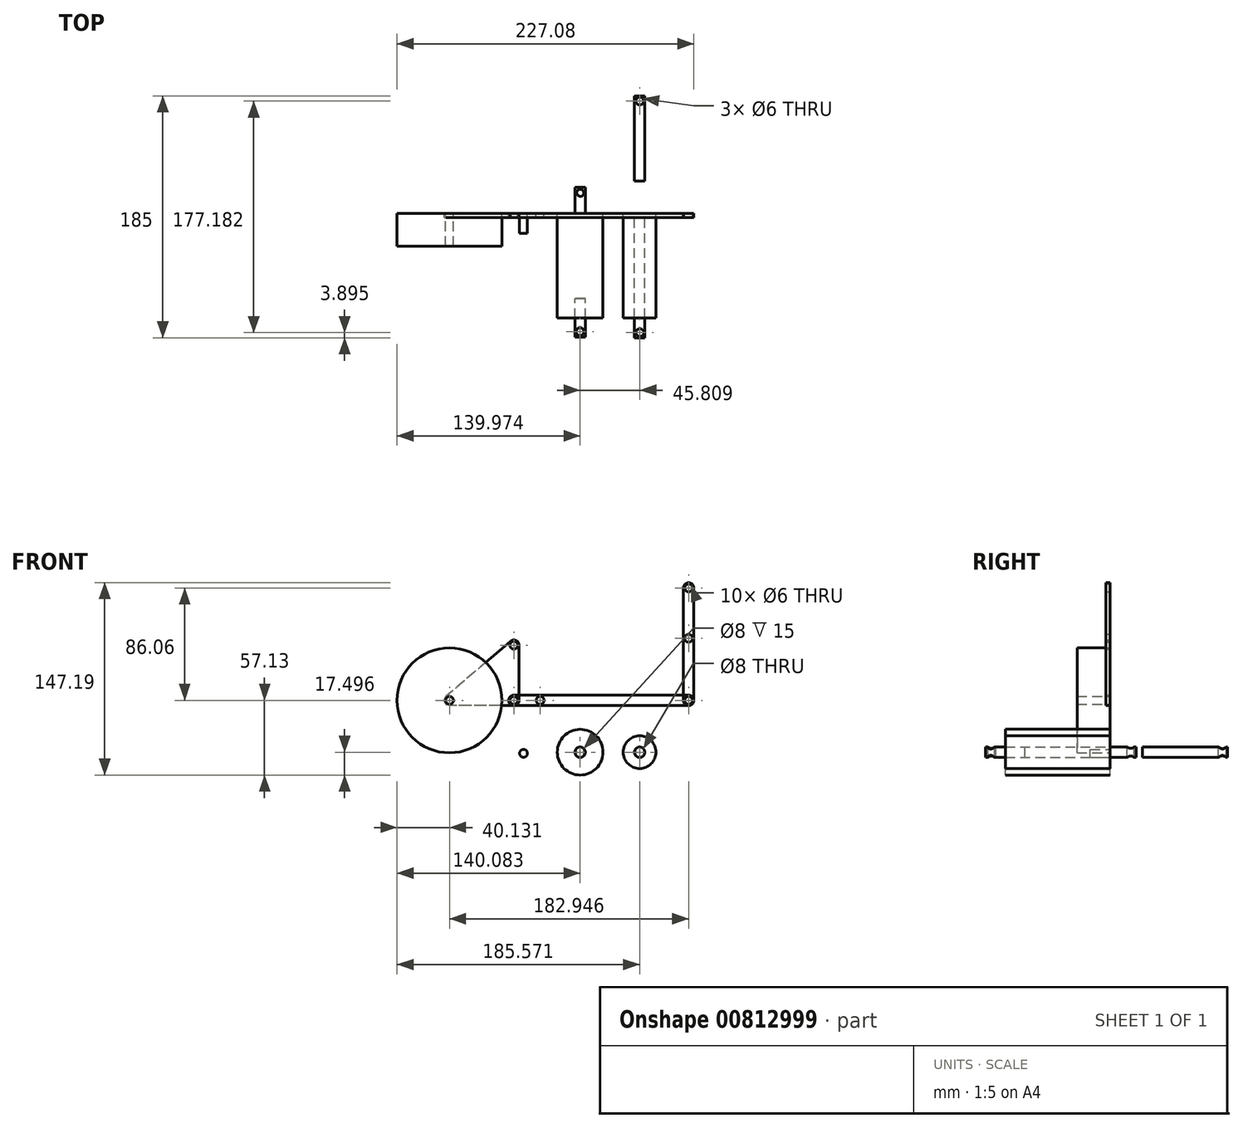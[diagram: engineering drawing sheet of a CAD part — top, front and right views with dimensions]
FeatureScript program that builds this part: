
annotation { "Feature Type Name" : "Feature", "Feature Type Description" : "" }
export const myFeature = defineFeature(function(context is Context, id is Id, definition is map)
    precondition{}
    {
        {
            var Q0;
            Q0=qCreatedBy(makeId("Front.planeOp"),FACE);
            var sketch = newSketch(context, id + "F0", { "sketchPlane" : qUnion([Q0])});
            skCircle(sketch, "E0", {"center": v(0, 0) * mm, "radius": 4 * mm});
            skCircle(sketch, "E1", {"center": v(-49.22, 0) * mm, "radius": 4 * mm});
            skCircle(sketch, "E2", {"center": v(0, 42.23) * mm, "radius": 4 * mm});
            skLineSegment(sketch, "E3", {"start": v(0, -4) * mm, "end": v(-49.22, -4) * mm});
            skLineSegment(sketch, "E4", {"start": v(4, 0) * mm, "end": v(4, 42.23) * mm});
            skLineSegment(sketch, "E5", {"start": v(-2.78, 45.1) * mm, "end": v(-51.82, 3.04) * mm});
            skCircle(sketch, "E6", {"center": v(0, 0) * mm, "radius": 3 * mm});
            skCircle(sketch, "E7", {"center": v(-49.22, 0) * mm, "radius": 3 * mm});
            skCircle(sketch, "E8", {"center": v(0, 42.23) * mm, "radius": 3 * mm});
            skLineSegment(sketch, "E9", {"start": v(0, 4) * mm, "end": v(133.73, 4) * mm});
            skLineSegment(sketch, "E10", {"start": v(0, -4) * mm, "end": v(133.73, -4) * mm});
            skCircle(sketch, "E11", {"center": v(133.73, 0) * mm, "radius": 4 * mm});
            skCircle(sketch, "E12", {"center": v(133.73, 0) * mm, "radius": 3 * mm});
            skCircle(sketch, "E13", {"center": v(-49.22, 0) * mm, "radius": 40.13 * mm});
            skLineSegment(sketch, "E14", {"start": v(137.73, 0) * mm, "end": v(137.73, 86.06) * mm});
            skLineSegment(sketch, "E15", {"start": v(129.73, 0) * mm, "end": v(129.73, 86.06) * mm});
            skCircle(sketch, "E16", {"center": v(133.73, 86.06) * mm, "radius": 4 * mm});
            skCircle(sketch, "E17", {"center": v(133.73, 86.06) * mm, "radius": 3 * mm});
            skCircle(sketch, "E18", {"center": v(133.73, 47.59) * mm, "radius": 3 * mm});
            skCircle(sketch, "E19", {"center": v(20.09, 0) * mm, "radius": 3 * mm});
            skLineSegment(sketch, "E20", {"start": v(20.09, 0) * mm, "end": v(133.73, 47.59) * mm, "construction": true});
            skLineSegment(sketch, "E21", {"start": v(0, 42.23) * mm, "end": v(133.73, 86.06) * mm, "construction": true});
            skCircle(sketch, "E22", {"center": v(50.73, -39.63) * mm, "radius": 4 * mm});
            skCircle(sketch, "E23", {"center": v(50.73, -39.63) * mm, "radius": 17.5 * mm});
            skCircle(sketch, "E24", {"center": v(7.4, -40.5) * mm, "radius": 3 * mm});
            skCircle(sketch, "E25", {"center": v(96.22, -39.63) * mm, "radius": 4 * mm});
            skCircle(sketch, "E26", {"center": v(96.22, -39.63) * mm, "radius": 12.5 * mm});
            skSolve(sketch);
        }
        {
            var Q0;
            Q0=makeQuery(id+"F0.imprint","IMPRINT",FACE,{"disambiguationData":[TD([[makeQuery(id+"F0.imprint","IMPRINT",EDGE,{"derivedFrom":sQuery(id+"F0.wireOp",EDGE,"E22")}),1.0]])]});
            var Q1;
            Q1=sQuery(id+"F0.wireOp",EDGE,"E22");
            extrude(context, id + "F1", {"entities" : qUnion([Q0]), "surfaceEntities" : qUnion([Q1]), "depth" : 65 * mm, "offsetDistance" : 25 * mm});
        }
        {
            var Q0;
            Q0=makeQuery(id+"F0.imprint","IMPRINT",FACE,{"disambiguationData":[TD([[makeQuery(id+"F0.imprint","IMPRINT",EDGE,{"derivedFrom":sQuery(id+"F0.wireOp",EDGE,"E22")}),-1.0]])]});
            extrude(context, id + "F2", {"entities" : qUnion([Q0]), "depth" : 80 * mm, "offsetDistance" : 25 * mm});
        }
        {
            var Q0;
            Q0=makeQuery(id+"F2.opExtrude","CAP_FACE",FACE,{"disambiguationData":[OSD([sQuery(id+"F0.wireOp",EDGE,"E22"),sQuery(id+"F0.wireOp",EDGE,"E23")])],"isStart":true});
            var sketch = newSketch(context, id + "F3", { "sketchPlane" : qUnion([Q0])});
            skCircle(sketch, "E27.0", {"center": v(-50.73, -39.63) * mm, "radius": 4 * mm});
            skSolve(sketch);
        }
        {
            var Q0;
            Q0 = qSketchRegion(id + "F3", true);
            extrude(context, id + "F4", {"entities" : qUnion([Q0]), "operationType" : NewBodyOperationType.ADD, "depth" : 20 * mm, "offsetDistance" : 25 * mm});
        }
        {
            var Q0;
            Q0=qCreatedBy(makeId("Top.planeOp"),FACE);
            var sketch = newSketch(context, id + "F5", { "sketchPlane" : qUnion([Q0])});
            skCircle(sketch, "E28", {"center": v(50.8, 15.89) * mm, "radius": 2.72 * mm});
            skSolve(sketch);
        }
        {
            var Q0;
            Q0 = qSketchRegion(id + "F5", true);
            extrude(context, id + "F6", {"entities" : qUnion([Q0]), "operationType" : NewBodyOperationType.REMOVE, "endBound" : BoundingType.THROUGH_ALL, "oppositeDirection" : true, "depth" : 25 * mm, "offsetDistance" : 25 * mm});
        }
        {
            var Q0;
            Q0=makeQuery(id+"F2.opExtrude","CAP_FACE",FACE,{"disambiguationData":[OSD([sQuery(id+"F0.wireOp",EDGE,"E22"),sQuery(id+"F0.wireOp",EDGE,"E23")])],"isStart":false});
            var sketch = newSketch(context, id + "F7", { "sketchPlane" : qUnion([Q0])});
            skSolve(sketch);
        }
        {
            var Q0;
            Q0=makeQuery(id+"F7.imprint","IMPRINT",FACE,{"disambiguationData":[TD([[makeQuery(id+"F7.imprint","IMPRINT",EDGE,{"derivedFrom":makeQuery(id+"F2.opExtrude","CAP_EDGE",EDGE,{"disambiguationData":[OSD([sQuery(id+"F0.wireOp",EDGE,"E22")])],"isStart":false})}),1.0]])]});
            extrude(context, id + "F8", {"entities" : qUnion([Q0]), "operationType" : NewBodyOperationType.ADD, "depth" : 14.5 * mm, "offsetDistance" : 25 * mm});
        }
        {
            var Q0;
            Q0=qCreatedBy(makeId("Top.planeOp"),FACE);
            var sketch = newSketch(context, id + "F9", { "sketchPlane" : qUnion([Q0])});
            skCircle(sketch, "E29", {"center": v(50.62, -90.32) * mm, "radius": 3 * mm});
            skSolve(sketch);
        }
        {
            var Q0;
            Q0 = qSketchRegion(id + "F9", true);
            extrude(context, id + "F10", {"entities" : qUnion([Q0]), "operationType" : NewBodyOperationType.REMOVE, "endBound" : BoundingType.THROUGH_ALL, "oppositeDirection" : true, "depth" : 25 * mm, "offsetDistance" : 25 * mm});
        }
        {
            var Q0;
            Q0=makeQuery(id+"F0.imprint","IMPRINT",FACE,{"disambiguationData":[TD([[makeQuery(id+"F0.imprint","IMPRINT",EDGE,{"derivedFrom":sQuery(id+"F0.wireOp",EDGE,"E24")}),1.0]])]});
            extrude(context, id + "F11", {"entities" : qUnion([Q0]), "depth" : 15 * mm, "offsetDistance" : 25 * mm});
        }
        {
            var Q0;
            Q0=makeQuery(id+"F0.imprint","IMPRINT",FACE,{"disambiguationData":[TD([[makeQuery(id+"F0.imprint","IMPRINT",EDGE,{"derivedFrom":sQuery(id+"F0.wireOp",EDGE,"E25")}),-1.0]])]});
            extrude(context, id + "F12", {"entities" : qUnion([Q0]), "depth" : 80 * mm, "offsetDistance" : 25 * mm});
        }
        {
            var Q0;
            Q0=makeQuery(id+"F12.opExtrude","CAP_FACE",FACE,{"disambiguationData":[OSD([sQuery(id+"F0.wireOp",EDGE,"E25"),sQuery(id+"F0.wireOp",EDGE,"E26")])],"isStart":false});
            var sketch = newSketch(context, id + "F13", { "sketchPlane" : qUnion([Q0])});
            skCircle(sketch, "E30.0", {"center": v(96.22, -39.63) * mm, "radius": 4 * mm});
            skSolve(sketch);
        }
        {
            var Q0;
            Q0 = qSketchRegion(id + "F13", true);
            extrude(context, id + "F14", {"entities" : qUnion([Q0]), "operationType" : NewBodyOperationType.ADD, "depth" : 15 * mm, "offsetDistance" : 25 * mm});
        }
        {
            var Q0;
            Q0=qCreatedBy(makeId("Top.planeOp"),FACE);
            var sketch = newSketch(context, id + "F15", { "sketchPlane" : qUnion([Q0])});
            skCircle(sketch, "E31", {"center": v(96.43, -91.1) * mm, "radius": 3 * mm});
            skSolve(sketch);
        }
        {
            var Q0;
            Q0 = qSketchRegion(id + "F15", true);
            extrude(context, id + "F16", {"entities" : qUnion([Q0]), "operationType" : NewBodyOperationType.REMOVE, "endBound" : BoundingType.THROUGH_ALL, "oppositeDirection" : true, "depth" : 25 * mm, "offsetDistance" : 25 * mm});
        }
        {
            var Q0;
            Q0=makeQuery(id+"F0.imprint","IMPRINT",FACE,{"disambiguationData":[TD([[makeQuery(id+"F0.imprint","IMPRINT",EDGE,{"derivedFrom":sQuery(id+"F0.wireOp",EDGE,"E25")}),1.0]])]});
            extrude(context, id + "F17", {"entities" : qUnion([Q0]), "oppositeDirection" : true, "depth" : 90 * mm, "offsetDistance" : 25 * mm, "hasSecondDirection" : true, "secondDirectionOppositeDirection" : true, "secondDirectionDepth" : 25 * mm});
        }
        {
            var Q0;
            Q0=qCreatedBy(makeId("Top.planeOp"),FACE);
            var sketch = newSketch(context, id + "F18", { "sketchPlane" : qUnion([Q0])});
            skCircle(sketch, "E32", {"center": v(96.37, 86.08) * mm, "radius": 3 * mm});
            skSolve(sketch);
        }
        {
            var Q0;
            Q0 = qSketchRegion(id + "F18", true);
            extrude(context, id + "F19", {"entities" : qUnion([Q0]), "operationType" : NewBodyOperationType.REMOVE, "endBound" : BoundingType.THROUGH_ALL, "oppositeDirection" : true, "depth" : 25 * mm, "offsetDistance" : 25 * mm});
        }
        {
            var Q0;
            Q0=makeQuery(id+"F0.imprint","IMPRINT",FACE,{"disambiguationData":[TD([[makeQuery(id+"F0.imprint","IMPRINT",EDGE,{"derivedFrom":sQuery(id+"F0.wireOp",EDGE,"E12")}),-1.0]])]});
            var Q1;
            {var subQ7=sQuery(id+"F0.wireOp",EDGE,"E14");Q1=makeQuery(id+"F0.imprint","IMPRINT",FACE,{"disambiguationData":[TD([[makeQuery(id+"F0.imprint","IMPRINT",EDGE,{"derivedFrom":subQ7}),1.0]])]});}
            var Q2;
            {var subQ0=sQuery(id+"F0.wireOp",EDGE,"E11");var subQ1=sQuery(id+"F0.wireOp",EDGE,"E9");var subQ2=makeQuery(id+"F0.imprint","INTERSECT",VERTEX,{"derivedFrom":[subQ1,subQ0]});Q2=makeQuery(id+"F0.imprint","IMPRINT",FACE,{"disambiguationData":[TD([[makeQuery(id+"F0.imprint","IMPRINT",EDGE,{"disambiguationData":[TD([[subQ2,1.0]])],"derivedFrom":subQ1}),-1.0]])]});}
            var Q3;
            Q3=makeQuery(id+"F0.imprint","IMPRINT",FACE,{"disambiguationData":[TD([[makeQuery(id+"F0.imprint","IMPRINT",EDGE,{"derivedFrom":sQuery(id+"F0.wireOp",EDGE,"E17")}),-1.0]])]});
            extrude(context, id + "F20", {"entities" : qUnion([Q0, Q1, Q2, Q3]), "depth" : 3 * mm, "offsetDistance" : 25 * mm});
        }
        {
            var Q0;
            Q0=makeQuery(id+"F0.imprint","IMPRINT",FACE,{"disambiguationData":[TD([[makeQuery(id+"F0.imprint","IMPRINT",EDGE,{"derivedFrom":sQuery(id+"F0.wireOp",EDGE,"E12")}),-1.0]])]});
            var Q1;
            {var subQ0=sQuery(id+"F0.wireOp",EDGE,"E11");var subQ1=sQuery(id+"F0.wireOp",EDGE,"E9");var subQ2=makeQuery(id+"F0.imprint","INTERSECT",VERTEX,{"derivedFrom":[subQ1,subQ0]});Q1=makeQuery(id+"F0.imprint","IMPRINT",FACE,{"disambiguationData":[TD([[makeQuery(id+"F0.imprint","IMPRINT",EDGE,{"disambiguationData":[TD([[subQ2,1.0]])],"derivedFrom":subQ1}),-1.0]])]});}
            var Q2;
            {var subQ0=sQuery(id+"F0.wireOp",EDGE,"E10");Q2=makeQuery(id+"F0.imprint","IMPRINT",FACE,{"disambiguationData":[TD([[makeQuery(id+"F0.imprint","IMPRINT",EDGE,{"derivedFrom":subQ0}),1.0]])]});}
            var Q3;
            {var subQ0=sQuery(id+"F0.wireOp",EDGE,"E4");var subQ1=sQuery(id+"F0.wireOp",EDGE,"E0");var subQ2=makeQuery(id+"F0.imprint","INTERSECT",VERTEX,{"derivedFrom":[subQ1,subQ0]});Q3=makeQuery(id+"F0.imprint","IMPRINT",FACE,{"disambiguationData":[TD([[makeQuery(id+"F0.imprint","IMPRINT",EDGE,{"disambiguationData":[TD([[subQ2,-1.0]])],"derivedFrom":subQ1}),-1.0]])]});}
            var Q4;
            Q4=makeQuery(id+"F0.imprint","IMPRINT",FACE,{"disambiguationData":[TD([[makeQuery(id+"F0.imprint","IMPRINT",EDGE,{"derivedFrom":sQuery(id+"F0.wireOp",EDGE,"E6")}),-1.0]])]});
            extrude(context, id + "F21", {"entities" : qUnion([Q0, Q1, Q2, Q3, Q4]), "depth" : 3 * mm, "offsetDistance" : 25 * mm});
        }
        {
            var Q0;
            {var subQ0=sQuery(id+"F0.wireOp",EDGE,"E4");var subQ1=sQuery(id+"F0.wireOp",EDGE,"E2");var subQ2=makeQuery(id+"F0.imprint","INTERSECT",VERTEX,{"derivedFrom":[subQ1,subQ0]});Q0=makeQuery(id+"F0.imprint","IMPRINT",FACE,{"disambiguationData":[TD([[makeQuery(id+"F0.imprint","IMPRINT",EDGE,{"disambiguationData":[TD([[subQ2,1.0]])],"derivedFrom":subQ1}),-1.0]])]});}
            var Q1;
            {var subQ0=sQuery(id+"F0.wireOp",EDGE,"E3");var subQ1=sQuery(id+"F0.wireOp",EDGE,"E1");var subQ2=makeQuery(id+"F0.imprint","INTERSECT",VERTEX,{"derivedFrom":[subQ1,subQ0]});Q1=makeQuery(id+"F0.imprint","IMPRINT",FACE,{"disambiguationData":[TD([[makeQuery(id+"F0.imprint","IMPRINT",EDGE,{"disambiguationData":[TD([[subQ2,-1.0]])],"derivedFrom":subQ1}),-1.0]])]});}
            var Q2;
            Q2=makeQuery(id+"F0.imprint","IMPRINT",FACE,{"disambiguationData":[TD([[makeQuery(id+"F0.imprint","IMPRINT",EDGE,{"derivedFrom":sQuery(id+"F0.wireOp",EDGE,"E7")}),-1.0]])]});
            var Q3;
            Q3=makeQuery(id+"F0.imprint","IMPRINT",FACE,{"disambiguationData":[TD([[makeQuery(id+"F0.imprint","IMPRINT",EDGE,{"derivedFrom":sQuery(id+"F0.wireOp",EDGE,"E6")}),-1.0]])]});
            var Q4;
            {var subQ0=sQuery(id+"F0.wireOp",EDGE,"E4");var subQ1=sQuery(id+"F0.wireOp",EDGE,"E0");var subQ2=makeQuery(id+"F0.imprint","INTERSECT",VERTEX,{"derivedFrom":[subQ1,subQ0]});Q4=makeQuery(id+"F0.imprint","IMPRINT",FACE,{"disambiguationData":[TD([[makeQuery(id+"F0.imprint","IMPRINT",EDGE,{"disambiguationData":[TD([[subQ2,-1.0]])],"derivedFrom":subQ1}),-1.0]])]});}
            var Q5;
            Q5=makeQuery(id+"F0.imprint","IMPRINT",FACE,{"disambiguationData":[TD([[makeQuery(id+"F0.imprint","IMPRINT",EDGE,{"derivedFrom":sQuery(id+"F0.wireOp",EDGE,"E8")}),-1.0]])]});
            extrude(context, id + "F22", {"entities" : qUnion([Q0, Q1, Q2, Q3, Q4, Q5]), "depth" : 3 * mm, "offsetDistance" : 25 * mm});
        }
        {
            var Q0;
            {var subQ0=sQuery(id+"F0.wireOp",EDGE,"E3");var subQ1=sQuery(id+"F0.wireOp",EDGE,"E1");var subQ2=makeQuery(id+"F0.imprint","INTERSECT",VERTEX,{"derivedFrom":[subQ1,subQ0]});Q0=makeQuery(id+"F0.imprint","IMPRINT",FACE,{"disambiguationData":[TD([[makeQuery(id+"F0.imprint","IMPRINT",EDGE,{"disambiguationData":[TD([[subQ2,1.0]])],"derivedFrom":subQ1}),-1.0]])]});}
            var Q1;
            {var subQ0=sQuery(id+"F0.wireOp",EDGE,"E3");var subQ1=sQuery(id+"F0.wireOp",EDGE,"E1");var subQ2=makeQuery(id+"F0.imprint","INTERSECT",VERTEX,{"derivedFrom":[subQ1,subQ0]});Q1=makeQuery(id+"F0.imprint","IMPRINT",FACE,{"disambiguationData":[TD([[makeQuery(id+"F0.imprint","IMPRINT",EDGE,{"disambiguationData":[TD([[subQ2,-1.0]])],"derivedFrom":subQ1}),-1.0]])]});}
            var Q2;
            Q2=makeQuery(id+"F0.imprint","IMPRINT",FACE,{"disambiguationData":[TD([[makeQuery(id+"F0.imprint","IMPRINT",EDGE,{"derivedFrom":sQuery(id+"F0.wireOp",EDGE,"E7")}),-1.0]])]});
            extrude(context, id + "F23", {"entities" : qUnion([Q0, Q1, Q2]), "depth" : 25 * mm, "offsetDistance" : 25 * mm});
        }
    });
